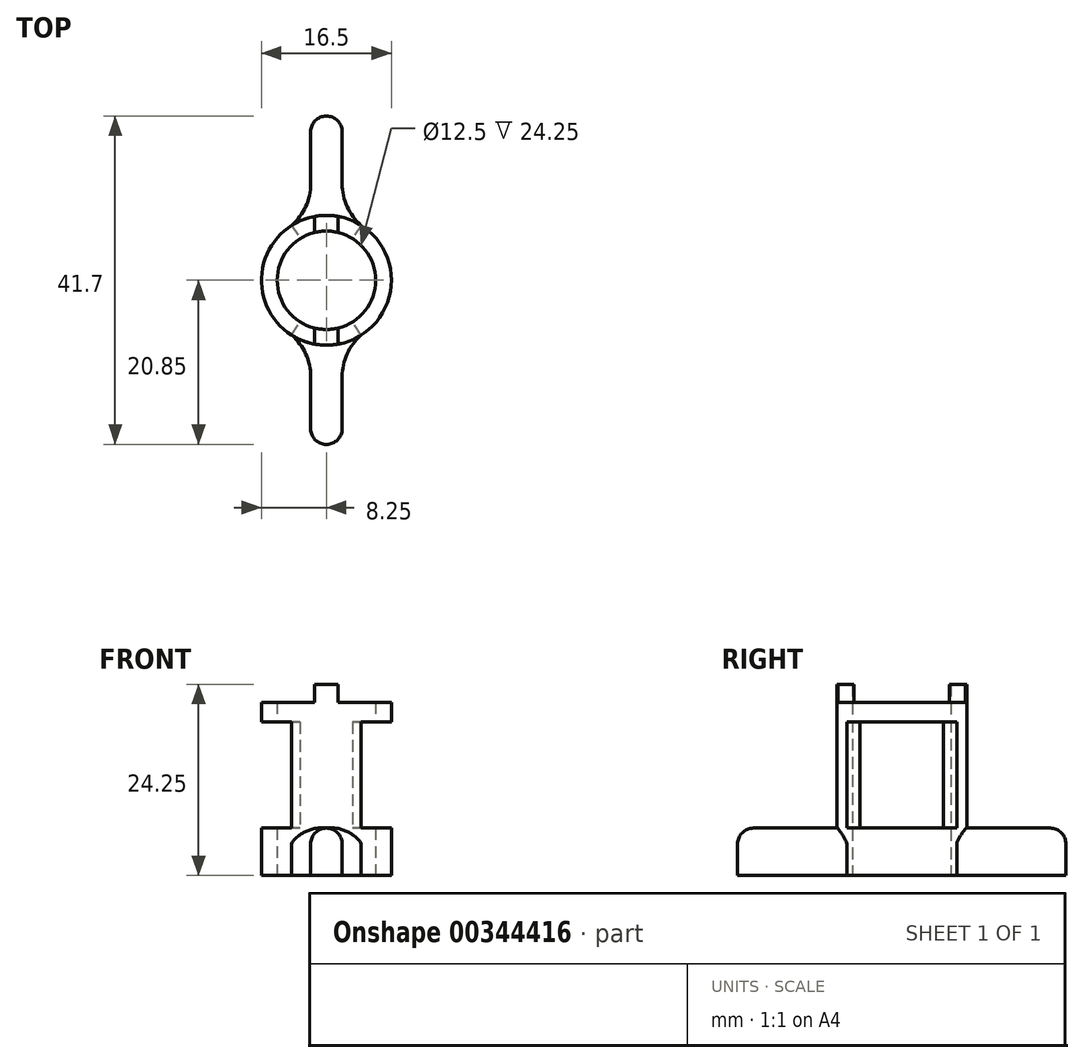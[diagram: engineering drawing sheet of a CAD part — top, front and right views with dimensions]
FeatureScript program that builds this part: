
annotation { "Feature Type Name" : "Feature", "Feature Type Description" : "" }
export const myFeature = defineFeature(function(context is Context, id is Id, definition is map)
    precondition{}
    {
        {
            var Q0;
            Q0=qCreatedBy(makeId("Top.planeOp"),FACE);
            var sketch = newSketch(context, id + "F0", { "sketchPlane" : qUnion([Q0])});
            skArc(sketch, "E0", {"start": v(-45.45, 0) * mm, "mid": v(-39.2, 6.25) * mm, "end": v(-32.95, 0) * mm});
            skArc(sketch, "E1", {"start": v(-47.45, 0) * mm, "mid": v(-46.42, 3.98) * mm, "end": v(-43.6, 6.98) * mm});
            skLineSegment(sketch, "E2", {"start": v(-39.2, 0) * mm, "end": v(-39.2, 20.85) * mm, "construction": true});
            skLineSegment(sketch, "E3", {"start": v(-39.2, 20.85) * mm, "end": v(-37.2, 20.85) * mm});
            skLineSegment(sketch, "E4", {"start": v(-39.2, 12.25) * mm, "end": v(-37.2, 12.25) * mm, "construction": true});
            skLineSegment(sketch, "E5", {"start": v(-37.2, 20.85) * mm, "end": v(-37.2, 12.25) * mm});
            skArc(sketch, "E6", {"start": v(-37.2, 12.25) * mm, "mid": v(-36.57, 9.35) * mm, "end": v(-34.8, 6.98) * mm});
            skLineSegment(sketch, "E7.MirrorCS", {"start": v(-41.2, 20.85) * mm, "end": v(-41.2, 12.25) * mm});
            skLineSegment(sketch, "E8.MirrorCS", {"start": v(-39.2, 20.85) * mm, "end": v(-41.2, 20.85) * mm});
            skArc(sketch, "E9.MirrorCS", {"start": v(-41.2, 12.25) * mm, "mid": v(-41.83, 9.35) * mm, "end": v(-43.6, 6.98) * mm});
            skArc(sketch, "E10.trimOffspring", {"start": v(-34.8, 6.98) * mm, "mid": v(-31.98, 3.98) * mm, "end": v(-30.95, 0) * mm});
            skLineSegment(sketch, "E11", {"start": v(-32.95, 0) * mm, "end": v(-30.95, 0) * mm});
            skLineSegment(sketch, "E12", {"start": v(-47.45, 0) * mm, "end": v(-45.45, 0) * mm});
            skSolve(sketch);
        }
        {
            var Q0;
            Q0=qSketchRegion(id+"F0",true);
            extrude(context, id + "F1", {"entities" : qUnion([Q0]), "depth" : 6 * mm});
        }
        {
            var Q0;
            Q0=makeQuery(id+"F1.opExtrude","CAP_FACE",FACE,{"disambiguationData":[OSD([sQuery(id+"F0.wireOp",EDGE,"E0"),sQuery(id+"F0.wireOp",EDGE,"E1"),sQuery(id+"F0.wireOp",EDGE,"E3"),sQuery(id+"F0.wireOp",EDGE,"E5"),sQuery(id+"F0.wireOp",EDGE,"E6"),sQuery(id+"F0.wireOp",EDGE,"E7.MirrorCS"),sQuery(id+"F0.wireOp",EDGE,"E8.MirrorCS"),sQuery(id+"F0.wireOp",EDGE,"E9.MirrorCS"),sQuery(id+"F0.wireOp",EDGE,"E10.trimOffspring"),sQuery(id+"F0.wireOp",EDGE,"3e348a9f-f184-40f3-a33d-7537a4a2d05c0.MirrorCS"),sQuery(id+"F0.wireOp",EDGE,"3e348a9f-f184-40f3-a33d-7537a4a2d05c1.MirrorCS"),sQuery(id+"F0.wireOp",EDGE,"3e348a9f-f184-40f3-a33d-7537a4a2d05c2.MirrorCS"),sQuery(id+"F0.wireOp",EDGE,"3e348a9f-f184-40f3-a33d-7537a4a2d05c3.MirrorCS"),sQuery(id+"F0.wireOp",EDGE,"3e348a9f-f184-40f3-a33d-7537a4a2d05c4.MirrorCS"),sQuery(id+"F0.wireOp",EDGE,"3e348a9f-f184-40f3-a33d-7537a4a2d05c5.MirrorCS"),sQuery(id+"F0.wireOp",EDGE,"3e348a9f-f184-40f3-a33d-7537a4a2d05c6.MirrorCS"),sQuery(id+"F0.wireOp",EDGE,"3e348a9f-f184-40f3-a33d-7537a4a2d05c7.MirrorCS"),sQuery(id+"F0.wireOp",EDGE,"3e348a9f-f184-40f3-a33d-7537a4a2d05c8.MirrorCS")])],"isStart":false});
            var sketch = newSketch(context, id + "F2", { "sketchPlane" : qUnion([Q0])});
            skLineSegment(sketch, "E13", {"start": v(-43.6, 6.98) * mm, "end": v(-42.53, 5.29) * mm});
            skLineSegment(sketch, "E14", {"start": v(-34.8, 6.98) * mm, "end": v(-35.87, 5.29) * mm});
            skLineSegment(sketch, "E15", {"start": v(-42.53, 5.29) * mm, "end": v(-39.2, 0) * mm, "construction": true});
            skLineSegment(sketch, "E16", {"start": v(-39.2, 0) * mm, "end": v(-35.87, 5.29) * mm, "construction": true});
            skArc(sketch, "E17", {"start": v(-42.53, 5.29) * mm, "mid": v(-39.2, 6.25) * mm, "end": v(-35.87, 5.29) * mm});
            skArc(sketch, "E18", {"start": v(-43.6, 6.98) * mm, "mid": v(-39.2, 8.25) * mm, "end": v(-34.8, 6.98) * mm});
            skSolve(sketch);
        }
        {
            var Q0;
            {var subQ0=sQuery(id+"F2.wireOp",EDGE,"E13");Q0=makeQuery(id+"F2.imprint","IMPRINT",FACE,{"disambiguationData":[TD([[makeQuery(id+"F2.imprint","IMPRINT",EDGE,{"derivedFrom":subQ0}),1.0]])]});}
            extrude(context, id + "F3", {"entities" : qUnion([Q0]), "operationType" : NewBodyOperationType.ADD, "depth" : 16 * mm});
        }
        {
            var Q0;
            Q0=makeQuery(id+"F3.opExtrude","CAP_FACE",FACE,{"disambiguationData":[OSD([sQuery(id+"F2.wireOp",EDGE,"E13"),sQuery(id+"F2.wireOp",EDGE,"E14"),sQuery(id+"F2.wireOp",EDGE,"E17"),sQuery(id+"F2.wireOp",EDGE,"E18")])],"isStart":false});
            var sketch = newSketch(context, id + "F4", { "sketchPlane" : qUnion([Q0])});
            skLineSegment(sketch, "E19", {"start": v(-39.2, 8.25) * mm, "end": v(-39.2, 6.25) * mm, "construction": true});
            skLineSegment(sketch, "E20", {"start": v(-40.7, 8.11) * mm, "end": v(-40.7, 6.07) * mm});
            skLineSegment(sketch, "E21", {"start": v(-37.7, 6.07) * mm, "end": v(-37.7, 8.11) * mm});
            skArc(sketch, "E22", {"start": v(-40.7, 8.11) * mm, "mid": v(-39.2, 8.25) * mm, "end": v(-37.7, 8.11) * mm});
            skArc(sketch, "E23", {"start": v(-40.7, 6.07) * mm, "mid": v(-39.2, 6.25) * mm, "end": v(-37.7, 6.07) * mm});
            skSolve(sketch);
        }
        {
            var Q0;
            Q0 = qSketchRegion(id + "F4", true);
            extrude(context, id + "F5", {"entities" : qUnion([Q0]), "operationType" : NewBodyOperationType.ADD, "depth" : 2.25 * mm});
        }
        {
            var Q0;
            Q0=makeQuery(id+"F1.opExtrude","CAP_EDGE",EDGE,{"disambiguationData":[OSD([sQuery(id+"F0.wireOp",EDGE,"E3"),sQuery(id+"F0.wireOp",EDGE,"E8.MirrorCS")])],"isStart":false});
            var Q1;
            Q1=makeQuery(id+"F1.opExtrude","SWEPT_EDGE",EDGE,{"disambiguationData":[OSD([sQuery(id+"F0.wireOp",EDGE,"E7.MirrorCS"),sQuery(id+"F0.wireOp",EDGE,"E8.MirrorCS")])]});
            var Q2;
            Q2=makeQuery(id+"F1.opExtrude","SWEPT_EDGE",EDGE,{"disambiguationData":[OSD([sQuery(id+"F0.wireOp",EDGE,"E3"),sQuery(id+"F0.wireOp",EDGE,"E5")])]});
            var Q3;
            Q3=makeQuery(id+"F1.opExtrude","CAP_EDGE",EDGE,{"disambiguationData":[OSD([sQuery(id+"F0.wireOp",EDGE,"E5")])],"isStart":false});
            var Q4;
            Q4=makeQuery(id+"F1.opExtrude","CAP_EDGE",EDGE,{"disambiguationData":[OSD([sQuery(id+"F0.wireOp",EDGE,"E7.MirrorCS")])],"isStart":false});
            fillet(context, id + "F6", {"entities" : qUnion([Q0, Q1, Q2, Q3, Q4]), "radius" : 2 * mm, "tangentPropagation" : true, "allowEdgeOverflow" : false});
        }
        {
            var Q0;
            {var subQ0=sQuery(id+"F2.wireOp",EDGE,"E17");var subQ1=sQuery(id+"F2.wireOp",EDGE,"E18");var subQ2=sQuery(id+"F2.wireOp",EDGE,"E13");Q0=makeQuery(id+"F5.boolean.opBoolean","SPLIT",FACE,{"disambiguationData":[TD([makeQuery(id+"F3.opExtrude","SWEPT_FACE",FACE,{"disambiguationData":[OSD([subQ2])]})])],"derivedFrom":makeQuery(id+"F3.opExtrude","CAP_FACE",FACE,{"disambiguationData":[OSD([subQ2,sQuery(id+"F2.wireOp",EDGE,"E14"),subQ0,subQ1])],"isStart":false})});}
            var sketch = newSketch(context, id + "F7", { "sketchPlane" : qUnion([Q0])});
            skArc(sketch, "E24", {"start": v(-47.45, 0) * mm, "mid": v(-39.2, 8.25) * mm, "end": v(-30.95, 0) * mm});
            skArc(sketch, "E25", {"start": v(-45.45, 0) * mm, "mid": v(-39.2, 6.25) * mm, "end": v(-32.95, 0) * mm});
            skLineSegment(sketch, "E26", {"start": v(-47.45, 0) * mm, "end": v(-45.45, 0) * mm});
            skLineSegment(sketch, "E27", {"start": v(-32.95, 0) * mm, "end": v(-30.95, 0) * mm});
            skSolve(sketch);
        }
        {
            var Q0;
            Q0 = qSketchRegion(id + "F7", true);
            extrude(context, id + "F8", {"entities" : qUnion([Q0]), "operationType" : NewBodyOperationType.ADD, "oppositeDirection" : true, "depth" : 2.5 * mm});
        }
        {
            var Q0;
            Q0=makeQuery(id+"F1.opExtrude","SWEPT_BODY",BODY,{"disambiguationData":[OSD([sQuery(id+"F0.wireOp",EDGE,"E0"),sQuery(id+"F0.wireOp",EDGE,"E1"),sQuery(id+"F0.wireOp",EDGE,"E3"),sQuery(id+"F0.wireOp",EDGE,"E5"),sQuery(id+"F0.wireOp",EDGE,"E6"),sQuery(id+"F0.wireOp",EDGE,"E7.MirrorCS"),sQuery(id+"F0.wireOp",EDGE,"E8.MirrorCS"),sQuery(id+"F0.wireOp",EDGE,"E9.MirrorCS"),sQuery(id+"F0.wireOp",EDGE,"E10.trimOffspring"),sQuery(id+"F0.wireOp",EDGE,"E11"),sQuery(id+"F0.wireOp",EDGE,"E12")])]});
            var Q1;
            Q1=qCreatedBy(makeId("Front.planeOp"),FACE);
            mirror(context, id + "F9", {"operationType" : NewBodyOperationType.ADD, "entities" : qUnion([Q0]), "mirrorPlane" : qUnion([Q1])});
        }
    });
